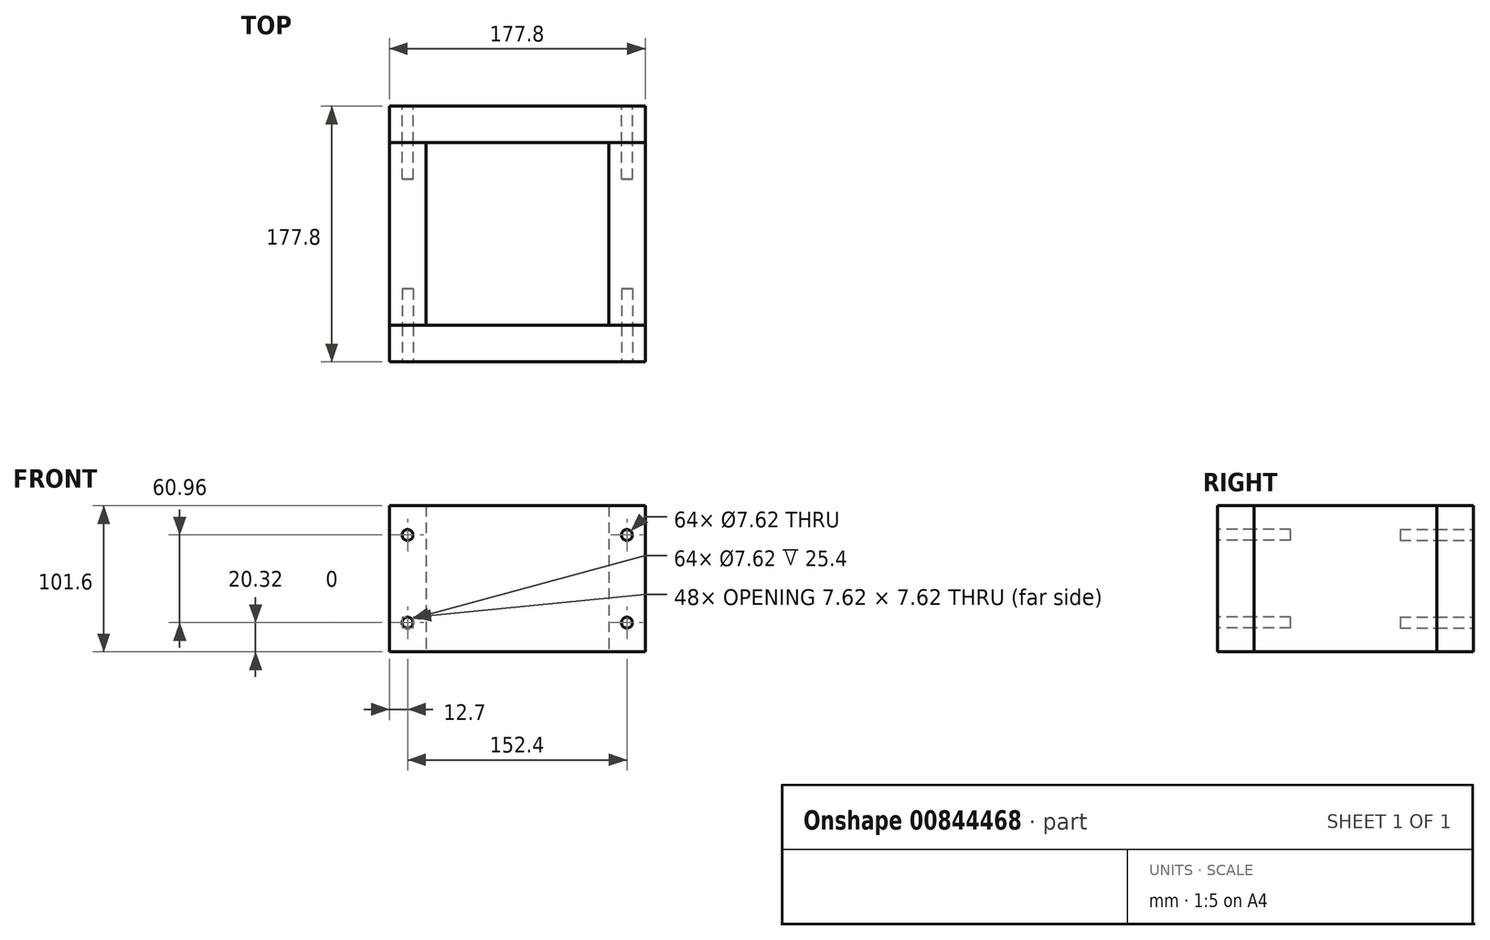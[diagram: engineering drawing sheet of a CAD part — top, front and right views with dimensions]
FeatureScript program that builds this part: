
annotation { "Feature Type Name" : "Feature", "Feature Type Description" : "" }
export const myFeature = defineFeature(function(context is Context, id is Id, definition is map)
    precondition{}
    {
        {
            var Q0;
            Q0=qCreatedBy(makeId("Top.planeOp"),FACE);
            var sketch = newSketch(context, id + "F0", { "sketchPlane" : qUnion([Q0])});
            skLineSegment(sketch, "E0", {"start": v(0, 0) * mm, "end": v(0, 127) * mm});
            skLineSegment(sketch, "E1", {"start": v(0, 127) * mm, "end": v(127, 127) * mm});
            skLineSegment(sketch, "E2", {"start": v(127, 127) * mm, "end": v(127, 0) * mm});
            skLineSegment(sketch, "E3", {"start": v(127, 0) * mm, "end": v(0, 0) * mm});
            skLineSegment(sketch, "E4", {"start": v(-25.4, 136.78) * mm, "end": v(-25.4, -25.4) * mm});
            skLineSegment(sketch, "E5", {"start": v(-25.4, 152.4) * mm, "end": v(152.4, 152.4) * mm});
            skLineSegment(sketch, "E6", {"start": v(152.4, 152.4) * mm, "end": v(152.4, -18.67) * mm});
            skLineSegment(sketch, "E7", {"start": v(152.4, -25.4) * mm, "end": v(-25.4, -25.4) * mm});
            skLineSegment(sketch, "E8", {"start": v(-25.4, 136.78) * mm, "end": v(-25.4, 152.4) * mm});
            skLineSegment(sketch, "E9", {"start": v(152.4, -18.67) * mm, "end": v(152.4, -25.4) * mm});
            skLineSegment(sketch, "E10", {"start": v(0, 127) * mm, "end": v(-25.4, 127) * mm});
            skLineSegment(sketch, "E11", {"start": v(0, 0) * mm, "end": v(-25.4, 0) * mm});
            skLineSegment(sketch, "E12", {"start": v(127, 0) * mm, "end": v(152.4, 0) * mm});
            skLineSegment(sketch, "E13", {"start": v(152.4, 0) * mm, "end": v(153.39, -1.66) * mm});
            skLineSegment(sketch, "E14", {"start": v(127, 127) * mm, "end": v(152.4, 127) * mm});
            skLineSegment(sketch, "E15", {"start": v(152.4, 127) * mm, "end": v(153.39, 124.85) * mm});
            skSolve(sketch);
        }
        {
            var Q0;
            Q0=makeQuery(id+"F0.imprint","IMPRINT",FACE,{"disambiguationData":[TD([[makeQuery(id+"F0.imprint","IMPRINT",EDGE,{"derivedFrom":sQuery(id+"F0.wireOp",EDGE,"E0")}),1.0]])]});
            var Q1;
            Q1=makeQuery(id+"F0.imprint","IMPRINT",FACE,{"disambiguationData":[TD([[makeQuery(id+"F0.imprint","IMPRINT",EDGE,{"derivedFrom":sQuery(id+"F0.wireOp",EDGE,"E2")}),1.0]])]});
            extrude(context, id + "F1", {"entities" : qUnion([Q0, Q1]), "depth" : 101.6 * mm, "offsetDistance" : 25.4 * mm});
        }
        {
            var Q0;
            Q0=makeQuery(id+"F0.imprint","IMPRINT",FACE,{"disambiguationData":[TD([[makeQuery(id+"F0.imprint","IMPRINT",EDGE,{"derivedFrom":sQuery(id+"F0.wireOp",EDGE,"E1")}),1.0]])]});
            var Q1;
            Q1=makeQuery(id+"F0.imprint","IMPRINT",FACE,{"disambiguationData":[TD([[makeQuery(id+"F0.imprint","IMPRINT",EDGE,{"derivedFrom":sQuery(id+"F0.wireOp",EDGE,"E3")}),1.0]])]});
            extrude(context, id + "F2", {"entities" : qUnion([Q0, Q1]), "depth" : 101.6 * mm, "offsetDistance" : 25.4 * mm});
        }
        {
            var Q0;
            Q0=makeQuery(id+"F2.opExtrude","SWEPT_FACE",FACE,{"disambiguationData":[OSD([sQuery(id+"F0.wireOp",EDGE,"E7")])]});
            var sketch = newSketch(context, id + "F3", { "sketchPlane" : qUnion([Q0])});
            skLineSegment(sketch, "E16", {"start": v(0, 101.6) * mm, "end": v(0, 0) * mm});
            skLineSegment(sketch, "E17", {"start": v(127, 0) * mm, "end": v(127, 101.6) * mm});
            skCircle(sketch, "E18", {"center": v(-12.7, 81.28) * mm, "radius": 3.81 * mm});
            skCircle(sketch, "E19", {"center": v(-12.7, 20.32) * mm, "radius": 3.81 * mm});
            skCircle(sketch, "E20", {"center": v(139.7, 81.28) * mm, "radius": 3.81 * mm});
            skCircle(sketch, "E21", {"center": v(139.7, 20.32) * mm, "radius": 3.81 * mm});
            skSolve(sketch);
        }
        {
            var Q0;
            Q0=makeQuery(id+"F3.imprint","IMPRINT",FACE,{"disambiguationData":[TD([[makeQuery(id+"F3.imprint","IMPRINT",EDGE,{"derivedFrom":sQuery(id+"F3.wireOp",EDGE,"E20")}),1.0]])]});
            var Q1;
            Q1=makeQuery(id+"F3.imprint","IMPRINT",FACE,{"disambiguationData":[TD([[makeQuery(id+"F3.imprint","IMPRINT",EDGE,{"derivedFrom":sQuery(id+"F3.wireOp",EDGE,"E21")}),1.0]])]});
            var Q2;
            Q2=makeQuery(id+"F3.imprint","IMPRINT",FACE,{"disambiguationData":[TD([[makeQuery(id+"F3.imprint","IMPRINT",EDGE,{"derivedFrom":sQuery(id+"F3.wireOp",EDGE,"E19")}),1.0]])]});
            var Q3;
            Q3=makeQuery(id+"F3.imprint","IMPRINT",FACE,{"disambiguationData":[TD([[makeQuery(id+"F3.imprint","IMPRINT",EDGE,{"derivedFrom":sQuery(id+"F3.wireOp",EDGE,"E18")}),1.0]])]});
            extrude(context, id + "F4", {"entities" : qUnion([Q0, Q1, Q2, Q3]), "operationType" : NewBodyOperationType.REMOVE, "oppositeDirection" : true, "depth" : 50.8 * mm, "offsetDistance" : 25.4 * mm});
        }
        {
            var Q0;
            Q0=makeQuery(id+"F2.opExtrude","SWEPT_FACE",FACE,{"disambiguationData":[OSD([sQuery(id+"F0.wireOp",EDGE,"E5")])]});
            var sketch = newSketch(context, id + "F5", { "sketchPlane" : qUnion([Q0])});
            skLineSegment(sketch, "E22", {"start": v(-127, 101.6) * mm, "end": v(-127, 0) * mm});
            skLineSegment(sketch, "E23", {"start": v(0, 0) * mm, "end": v(0, 101.6) * mm});
            skCircle(sketch, "E24", {"center": v(-139.7, 81.28) * mm, "radius": 3.81 * mm});
            skCircle(sketch, "E25", {"center": v(-139.7, 20.32) * mm, "radius": 3.81 * mm});
            skCircle(sketch, "E26", {"center": v(12.7, 81.28) * mm, "radius": 3.81 * mm});
            skCircle(sketch, "E27", {"center": v(12.7, 20.32) * mm, "radius": 3.81 * mm});
            skSolve(sketch);
        }
        {
            var Q0;
            Q0=makeQuery(id+"F5.imprint","IMPRINT",FACE,{"disambiguationData":[TD([[makeQuery(id+"F5.imprint","IMPRINT",EDGE,{"derivedFrom":sQuery(id+"F5.wireOp",EDGE,"E24")}),1.0]])]});
            var Q1;
            Q1=makeQuery(id+"F5.imprint","IMPRINT",FACE,{"disambiguationData":[TD([[makeQuery(id+"F5.imprint","IMPRINT",EDGE,{"derivedFrom":sQuery(id+"F5.wireOp",EDGE,"E25")}),1.0]])]});
            var Q2;
            Q2=makeQuery(id+"F5.imprint","IMPRINT",FACE,{"disambiguationData":[TD([[makeQuery(id+"F5.imprint","IMPRINT",EDGE,{"derivedFrom":sQuery(id+"F5.wireOp",EDGE,"E27")}),1.0]])]});
            var Q3;
            Q3=makeQuery(id+"F5.imprint","IMPRINT",FACE,{"disambiguationData":[TD([[makeQuery(id+"F5.imprint","IMPRINT",EDGE,{"derivedFrom":sQuery(id+"F5.wireOp",EDGE,"E26")}),1.0]])]});
            extrude(context, id + "F6", {"entities" : qUnion([Q0, Q1, Q2, Q3]), "operationType" : NewBodyOperationType.REMOVE, "oppositeDirection" : true, "depth" : 50.8 * mm, "offsetDistance" : 25.4 * mm});
        }
    });
